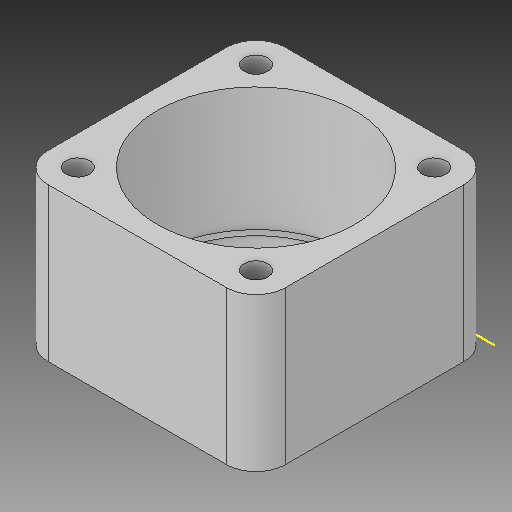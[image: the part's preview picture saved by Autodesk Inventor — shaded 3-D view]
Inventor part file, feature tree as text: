
AUTODESK INVENTOR PART (.ipt)
format: ipt  version: 2018 (Build 220112000, 112)  size: 267,776 bytes
history: native  units: in
note: dims shown in document units (in); Inventor stores cm internally (conversion verified against a paired STEP export)
features: extrude x10, sketch x9, fillet x2, hole x2, pattern_circular x1, projected_geometry x1
ambient origin geometry x8: Origin, YZ Plane, XZ Plane, XY Plane, X Axis, Y Axis, Z Axis, Center Point
bodies: Solid1 (feature_tree)
feature tree (25):
  sketch  "Sketch1"  dims[d0=3.325in d2=2.0in]
  extrude  "Extrusion1"  Depth=2.0in
  extrude  "Extrusion2"  Depth=2.081in TaperAngle=0.0deg
  extrude  "Extrusion3"  Depth=0.125in
  pattern_circular  "Circular Pattern1"  [2 undecoded]
  extrude  "Extrusion4"  Depth=0.125in
  sketch  "Sketch4"  dims[d3=2.0in d4=2.081in d5=0.0in]
  extrude  "Extrusion7"  Depth=0.25in
  extrude  "Extrusion8"  Depth=0.5in TaperAngle=0.0deg
  sketch  "Sketch7"  dims[d9=0.125in]
  fillet  "Fillet1"  Radius=0.5in
  extrude  "Extrusion11"  Depth=0.5in TaperAngle=360.0deg
  extrude  "Extrusion12"  Depth=0.5in TaperAngle=0.0deg
  hole  "Hole2"  [1 undecoded]
  sketch  "Sketch17"  dims[d13=0.125in d14=0.125in d15=0.125in d16=0.25in d17=0.5in d18=0.0in d19=0.5in d20=0.0in d21=1.5748in d22=360.0deg d24=0.5in d25=0.0in d30=0.625in d31=0.21in d32=0.0in d33=0.525in d34=0.2in d35=0.0in d43=0.125in d47=0.2in d48=0.0in d49=0.2in d50=0.0in d51=0.397in d52=0.75in d53=0.375in d54=0.25in d55=0.5635in d56=1.0in d57=0.0in d66=0.25in d67=0.0in d68=0.25in d69=0.0in d70=0.5in]
  extrude  "Extrusion15"  Depth=0.21in TaperAngle=0.0deg
  extrude  "Extrusion16"  Depth=0.5in
  fillet  "Fillet3"  Radius=0.2in
  projected_geometry  "Projected Loop3"
  sketch  "Sketch5"  dims[d6=0.125in d7=0.125in]
  sketch  "Sketch6"  dims[d8=0.125in]
  sketch  "Sketch11"  dims[d10=0.125in]
  sketch  "Sketch12"  dims[d11=0.125in]
  sketch  "Sketch13"  dims[d12=0.125in]
  hole  "Hole1"  [1 undecoded]
note: 4 required parameter values undecoded (feature->parameter linkage not recoverable at this tier; creation-order binding heuristic only, values carry confidence <= 0.55)
